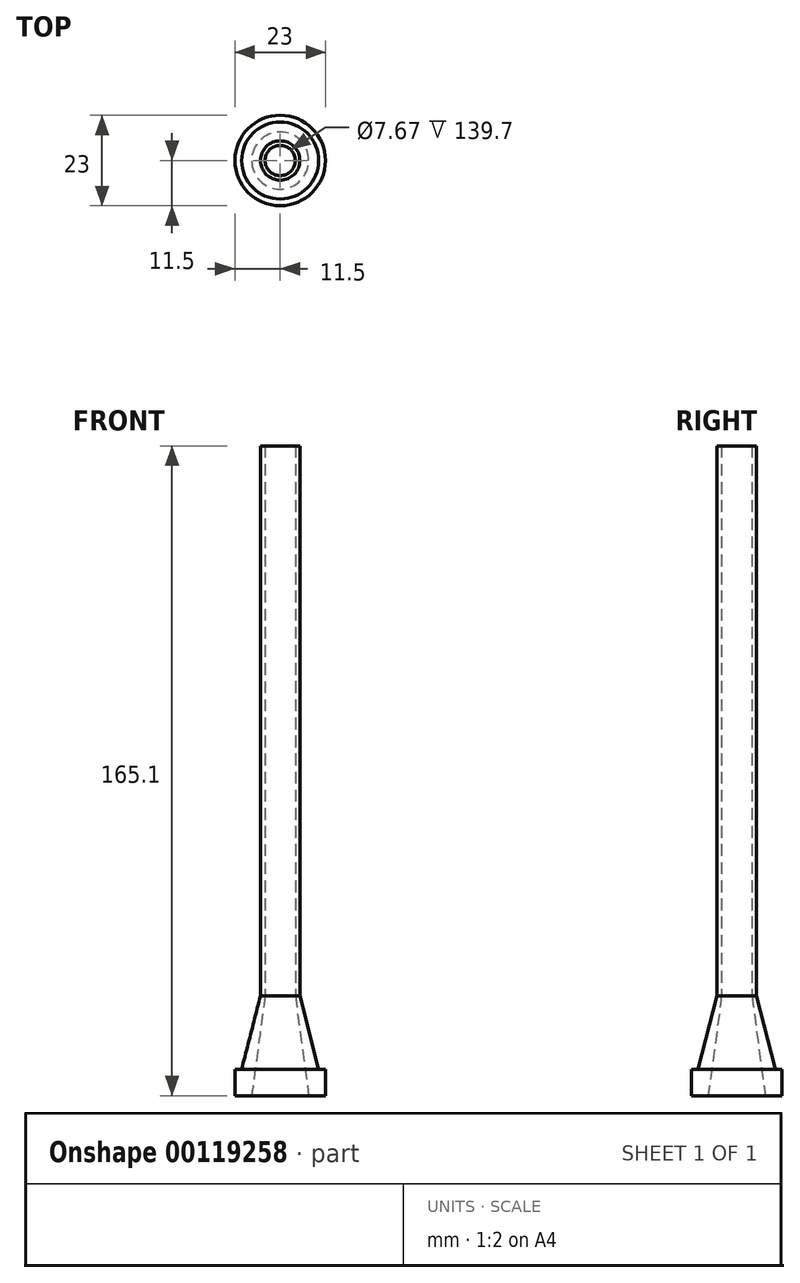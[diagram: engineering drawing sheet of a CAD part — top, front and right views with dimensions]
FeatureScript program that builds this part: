
annotation { "Feature Type Name" : "Feature", "Feature Type Description" : "" }
export const myFeature = defineFeature(function(context is Context, id is Id, definition is map)
    precondition{}
    {
        {
            var Q0;
            Q0=qCreatedBy(makeId("Front.planeOp"),FACE);
            var sketch = newSketch(context, id + "F0", { "sketchPlane" : qUnion([Q0])});
            skLineSegment(sketch, "E0", {"start": v(0, 0) * mm, "end": v(11.5, 0) * mm});
            skLineSegment(sketch, "E1", {"start": v(0, 0) * mm, "end": v(0, 25.4) * mm});
            skLineSegment(sketch, "E2", {"start": v(3.84, 25.4) * mm, "end": v(5, 25.4) * mm});
            skLineSegment(sketch, "E3", {"start": v(5, 25.4) * mm, "end": v(11.5, 0) * mm});
            skLineSegment(sketch, "E4", {"start": v(7.25, 0) * mm, "end": v(3.84, 25.4) * mm});
            skLineSegment(sketch, "E5", {"start": v(3.84, 25.4) * mm, "end": v(3.84, 165.1) * mm});
            skLineSegment(sketch, "E6", {"start": v(5, 25.4) * mm, "end": v(5, 165.1) * mm});
            skLineSegment(sketch, "E7", {"start": v(5, 165.1) * mm, "end": v(3.84, 165.1) * mm});
            skLineSegment(sketch, "E8", {"start": v(11.5, 0) * mm, "end": v(11.5, 6.66) * mm});
            skLineSegment(sketch, "E9", {"start": v(11.5, 6.66) * mm, "end": v(9.8, 6.66) * mm});
            skSolve(sketch);
        }
        {
            var Q0;
            {var subQ0=sQuery(id+"F0.wireOp",EDGE,"E8");Q0=makeQuery(id+"F0.imprint","IMPRINT",FACE,{"disambiguationData":[TD([[makeQuery(id+"F0.imprint","IMPRINT",EDGE,{"derivedFrom":subQ0}),1.0]])]});}
            var Q1;
            {var subQ4=sQuery(id+"F0.wireOp",EDGE,"E2");Q1=makeQuery(id+"F0.imprint","IMPRINT",FACE,{"disambiguationData":[TD([[makeQuery(id+"F0.imprint","IMPRINT",EDGE,{"derivedFrom":subQ4}),-1.0]])]});}
            var Q2;
            Q2=makeQuery(id+"F0.imprint","IMPRINT",FACE,{"disambiguationData":[TD([[makeQuery(id+"F0.imprint","IMPRINT",EDGE,{"derivedFrom":sQuery(id+"F0.wireOp",EDGE,"E2")}),1.0]])]});
            var Q3;
            Q3=sQuery(id+"F0.wireOp",EDGE,"E1");
            revolve(context, id + "F1", {"entities" : qUnion([Q0, Q1, Q2]), "axis" : qUnion([Q3]), "revolveType" : RevolveType.FULL});
        }
    });
